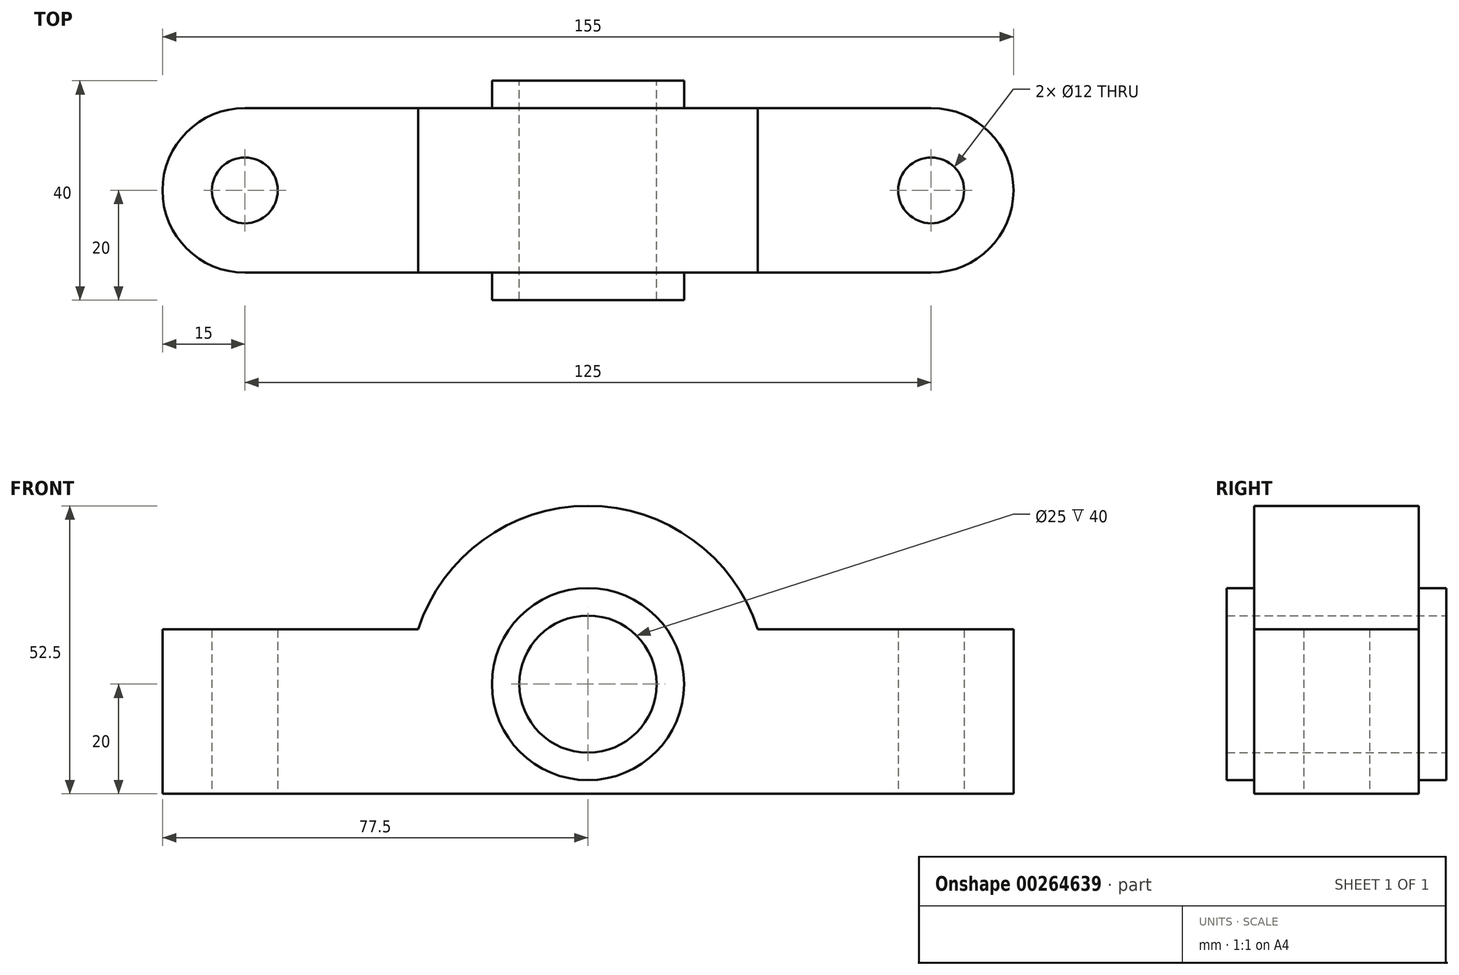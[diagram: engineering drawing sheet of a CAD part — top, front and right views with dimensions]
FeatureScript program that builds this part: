
annotation { "Feature Type Name" : "Feature", "Feature Type Description" : "" }
export const myFeature = defineFeature(function(context is Context, id is Id, definition is map)
    precondition{}
    {
        {
            var Q0;
            Q0=qCreatedBy(makeId("Front.planeOp"),FACE);
            var sketch = newSketch(context, id + "F0", { "sketchPlane" : qUnion([Q0])});
            skLineSegment(sketch, "E0", {"start": v(0, 0) * mm, "end": v(-116.44, 0) * mm});
            skLineSegment(sketch, "E1", {"start": v(-116.44, 0) * mm, "end": v(-116.44, 20) * mm});
            skLineSegment(sketch, "E2", {"start": v(-116.44, 20) * mm, "end": v(-12.5, 20) * mm});
            skLineSegment(sketch, "E3", {"start": v(12.5, 20) * mm, "end": v(116.44, 20) * mm});
            skLineSegment(sketch, "E4", {"start": v(116.44, 20) * mm, "end": v(116.44, 0) * mm});
            skLineSegment(sketch, "E5", {"start": v(116.44, 0) * mm, "end": v(0, 0) * mm});
            skLineSegment(sketch, "E6", {"start": v(-116.44, 20) * mm, "end": v(-116.44, 30) * mm});
            skLineSegment(sketch, "E7", {"start": v(-116.44, 30) * mm, "end": v(-30.92, 30) * mm});
            skLineSegment(sketch, "E8", {"start": v(30.92, 30) * mm, "end": v(116.44, 30) * mm});
            skLineSegment(sketch, "E9", {"start": v(116.44, 30) * mm, "end": v(116.44, 20) * mm});
            skCircle(sketch, "E10", {"center": v(0, 20) * mm, "radius": 12.5 * mm});
            skArc(sketch, "E11", {"start": v(30.92, 30) * mm, "mid": v(0, 52.5) * mm, "end": v(-30.92, 30) * mm});
            skCircle(sketch, "E12", {"center": v(0, 20) * mm, "radius": 17.5 * mm});
            skSolve(sketch);
        }
        {
            var Q0;
            Q0=qCreatedBy(makeId("Top.planeOp"),FACE);
            var sketch = newSketch(context, id + "F1", { "sketchPlane" : qUnion([Q0])});
            skCircle(sketch, "E13", {"center": v(-62.5, 0) * mm, "radius": 6 * mm});
            skCircle(sketch, "E14", {"center": v(62.5, 0) * mm, "radius": 6 * mm});
            skLineSegment(sketch, "E15", {"start": v(-62.5, 0) * mm, "end": v(0, 0) * mm, "construction": true});
            skLineSegment(sketch, "E16", {"start": v(0, 0) * mm, "end": v(62.5, 0) * mm, "construction": true});
            skArc(sketch, "E17", {"start": v(-62.5, 15) * mm, "mid": v(-77.5, 0) * mm, "end": v(-62.5, -15) * mm});
            skArc(sketch, "E18", {"start": v(62.5, -15) * mm, "mid": v(77.5, 0) * mm, "end": v(62.5, 15) * mm});
            skLineSegment(sketch, "E19", {"start": v(-62.5, -15) * mm, "end": v(62.5, -15) * mm});
            skLineSegment(sketch, "E20", {"start": v(62.5, 15) * mm, "end": v(-62.5, 15) * mm});
            skSolve(sketch);
        }
        {
            var Q0;
            Q0=makeQuery(id+"F0.imprint","IMPRINT",FACE,{"disambiguationData":[TD([[makeQuery(id+"F0.imprint","IMPRINT",EDGE,{"derivedFrom":sQuery(id+"F0.wireOp",EDGE,"E0")}),-1.0]])]});
            extrude(context, id + "F2", {"entities" : qUnion([Q0]), "endBound" : BoundingType.SYMMETRIC, "depth" : 43 * mm});
        }
        {
            var Q0;
            {var subQ0=sQuery(id+"F0.wireOp",EDGE,"E6");Q0=makeQuery(id+"F0.imprint","IMPRINT",FACE,{"disambiguationData":[TD([[makeQuery(id+"F0.imprint","IMPRINT",EDGE,{"derivedFrom":subQ0}),-1.0]])]});}
            extrude(context, id + "F3", {"entities" : qUnion([Q0]), "endBound" : BoundingType.SYMMETRIC, "depth" : 47.8 * mm});
        }
        {
            var Q0;
            Q0=makeQuery(id+"F1.imprint","IMPRINT",FACE,{"disambiguationData":[TD([[makeQuery(id+"F1.imprint","IMPRINT",EDGE,{"derivedFrom":sQuery(id+"F1.wireOp",EDGE,"E13")}),-1.0]])]});
            extrude(context, id + "F4", {"entities" : qUnion([Q0]), "operationType" : NewBodyOperationType.INTERSECT, "depth" : 69.6 * mm});
        }
        {
            var Q0;
            {var subQ0=sQuery(id+"F0.wireOp",EDGE,"E10");var subQ1=sQuery(id+"F0.wireOp",EDGE,"E2");var subQ2=makeQuery(id+"F0.imprint","INTERSECT",VERTEX,{"derivedFrom":[subQ1,subQ0]});Q0=makeQuery(id+"F0.imprint","IMPRINT",FACE,{"disambiguationData":[TD([[makeQuery(id+"F0.imprint","IMPRINT",EDGE,{"disambiguationData":[TD([[subQ2,1.0]])],"derivedFrom":subQ1}),-1.0]])]});}
            extrude(context, id + "F5", {"entities" : qUnion([Q0]), "operationType" : NewBodyOperationType.ADD, "endBound" : BoundingType.SYMMETRIC, "depth" : 40 * mm});
        }
        {
            var Q0;
            {var subQ0=sQuery(id+"F0.wireOp",EDGE,"E10");var subQ1=sQuery(id+"F0.wireOp",EDGE,"E2");var subQ2=makeQuery(id+"F0.imprint","INTERSECT",VERTEX,{"derivedFrom":[subQ1,subQ0]});Q0=makeQuery(id+"F0.imprint","IMPRINT",FACE,{"disambiguationData":[TD([[makeQuery(id+"F0.imprint","IMPRINT",EDGE,{"disambiguationData":[TD([[subQ2,1.0]])],"derivedFrom":subQ1}),1.0]])]});}
            extrude(context, id + "F6", {"entities" : qUnion([Q0]), "operationType" : NewBodyOperationType.ADD, "endBound" : BoundingType.SYMMETRIC, "depth" : 40 * mm});
        }
    });
